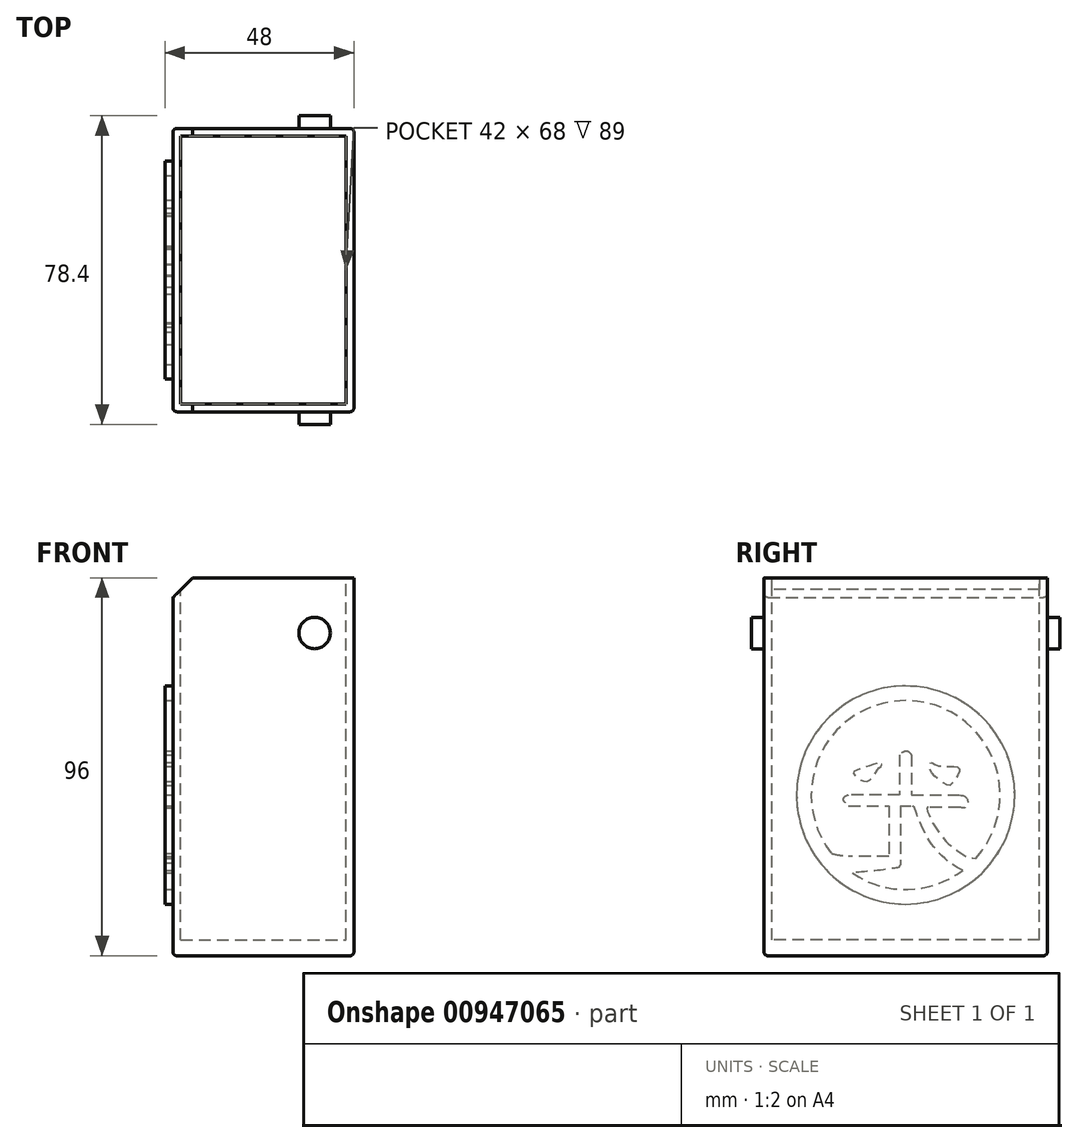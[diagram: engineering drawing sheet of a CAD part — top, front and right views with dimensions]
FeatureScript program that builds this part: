
annotation { "Feature Type Name" : "Feature", "Feature Type Description" : "" }
export const myFeature = defineFeature(function(context is Context, id is Id, definition is map)
    precondition{}
    {
        {
            var Q0;
            Q0=qCreatedBy(makeId("Top.planeOp"),FACE);
            var sketch = newSketch(context, id + "F0", { "sketchPlane" : qUnion([Q0])});
            skLineSegment(sketch, "E0.bottom", {"start": v(-23, 36) * mm, "end": v(23, 36) * mm});
            skLineSegment(sketch, "E0.top", {"start": v(-23, -36) * mm, "end": v(23, -36) * mm});
            skLineSegment(sketch, "E0.left", {"start": v(-23, 36) * mm, "end": v(-23, -36) * mm});
            skLineSegment(sketch, "E0.right", {"start": v(23, 36) * mm, "end": v(23, -36) * mm});
            skPoint(sketch, "E0.middle", {"position": v(0, 0) * mm});
            skSolve(sketch);
        }
        {
            var Q0;
            Q0 = qSketchRegion(id + "F0", true);
            extrude(context, id + "F1", {"entities" : qUnion([Q0]), "depth" : 96 * mm, "offsetDistance" : 25 * mm});
        }
        {
            var Q0;
            Q0=makeQuery(id+"F1.opExtrude","CAP_FACE",FACE,{"disambiguationData":[OSD([sQuery(id+"F0.wireOp",EDGE,"E0.bottom"),sQuery(id+"F0.wireOp",EDGE,"E0.top"),sQuery(id+"F0.wireOp",EDGE,"E0.left"),sQuery(id+"F0.wireOp",EDGE,"E0.right")])],"isStart":false});
            var sketch = newSketch(context, id + "F2", { "sketchPlane" : qUnion([Q0])});
            skLineSegment(sketch, "E1.bottom", {"start": v(-21, 34) * mm, "end": v(21, 34) * mm});
            skLineSegment(sketch, "E1.top", {"start": v(-21, -34) * mm, "end": v(21, -34) * mm});
            skLineSegment(sketch, "E1.left", {"start": v(-21, 34) * mm, "end": v(-21, -34) * mm});
            skLineSegment(sketch, "E1.right", {"start": v(21, 34) * mm, "end": v(21, -34) * mm});
            skPoint(sketch, "E1.middle", {"position": v(0, 0) * mm});
            skSolve(sketch);
        }
        {
            var Q0;
            Q0=makeQuery(id+"F2.imprint","IMPRINT",FACE,{"disambiguationData":[TD([[makeQuery(id+"F2.imprint","IMPRINT",EDGE,{"derivedFrom":sQuery(id+"F2.wireOp",EDGE,"E1.bottom")}),-1.0]])]});
            extrude(context, id + "F3", {"entities" : qUnion([Q0]), "operationType" : NewBodyOperationType.REMOVE, "oppositeDirection" : true, "depth" : 92 * mm, "offsetDistance" : 25 * mm});
        }
        {
            var Q0;
            Q0=makeQuery(id+"F1.opExtrude","SWEPT_FACE",FACE,{"disambiguationData":[OSD([sQuery(id+"F0.wireOp",EDGE,"E0.top")])]});
            var sketch = newSketch(context, id + "F4", { "sketchPlane" : qUnion([Q0])});
            skCircle(sketch, "E2", {"center": v(13, 82) * mm, "radius": 4 * mm});
            skSolve(sketch);
        }
        {
            var Q0;
            Q0 = qSketchRegion(id + "F4", true);
            extrude(context, id + "F5", {"entities" : qUnion([Q0]), "operationType" : NewBodyOperationType.ADD, "depth" : 3.2 * mm, "offsetDistance" : 25 * mm});
        }
        {
            var Q0;
            Q0=makeQuery(id+"F1.opExtrude","SWEPT_FACE",FACE,{"disambiguationData":[OSD([sQuery(id+"F0.wireOp",EDGE,"E0.bottom")])]});
            var sketch = newSketch(context, id + "F6", { "sketchPlane" : qUnion([Q0])});
            skCircle(sketch, "E3", {"center": v(-13, 82) * mm, "radius": 4 * mm});
            skSolve(sketch);
        }
        {
            var Q0;
            Q0 = qSketchRegion(id + "F6", true);
            extrude(context, id + "F7", {"entities" : qUnion([Q0]), "operationType" : NewBodyOperationType.ADD, "depth" : 3.2 * mm, "offsetDistance" : 25 * mm});
        }
        {
            var Q0;
            Q0=makeQuery(id+"F1.opExtrude","CAP_EDGE",EDGE,{"disambiguationData":[OSD([sQuery(id+"F0.wireOp",EDGE,"E0.left")])],"isStart":false});
            chamfer(context, id + "F8", {"entities" : qUnion([Q0]), "width" : 5 * mm, "tangentPropagation" : true});
        }
        {
            var Q0;
            Q0=makeQuery(id+"F1.opExtrude","SWEPT_EDGE",EDGE,{"disambiguationData":[OSD([sQuery(id+"F0.wireOp",EDGE,"E0.top"),sQuery(id+"F0.wireOp",EDGE,"E0.left")])]});
            var Q1;
            Q1=makeQuery(id+"F1.opExtrude","SWEPT_EDGE",EDGE,{"disambiguationData":[OSD([sQuery(id+"F0.wireOp",EDGE,"E0.top"),sQuery(id+"F0.wireOp",EDGE,"E0.right")])]});
            var Q2;
            Q2=makeQuery(id+"F1.opExtrude","SWEPT_EDGE",EDGE,{"disambiguationData":[OSD([sQuery(id+"F0.wireOp",EDGE,"E0.bottom"),sQuery(id+"F0.wireOp",EDGE,"E0.right")])]});
            var Q3;
            Q3=makeQuery(id+"F1.opExtrude","SWEPT_EDGE",EDGE,{"disambiguationData":[OSD([sQuery(id+"F0.wireOp",EDGE,"E0.bottom"),sQuery(id+"F0.wireOp",EDGE,"E0.left")])]});
            var Q4;
            Q4=makeQuery(id+"F1.opExtrude","CAP_EDGE",EDGE,{"disambiguationData":[OSD([sQuery(id+"F0.wireOp",EDGE,"E0.right")])],"isStart":true});
            var Q5;
            Q5=makeQuery(id+"F1.opExtrude","CAP_EDGE",EDGE,{"disambiguationData":[OSD([sQuery(id+"F0.wireOp",EDGE,"E0.left")])],"isStart":true});
            var Q6;
            Q6=makeQuery(id+"F1.opExtrude","CAP_EDGE",EDGE,{"disambiguationData":[OSD([sQuery(id+"F0.wireOp",EDGE,"E0.bottom")])],"isStart":true});
            var Q7;
            Q7=makeQuery(id+"F1.opExtrude","CAP_EDGE",EDGE,{"disambiguationData":[OSD([sQuery(id+"F0.wireOp",EDGE,"E0.top")])],"isStart":true});
            fillet(context, id + "F9", {"entities" : qUnion([Q0, Q1, Q2, Q3, Q4, Q5, Q6, Q7]), "radius" : 1 * mm, "tangentPropagation" : true, "allowEdgeOverflow" : false});
        }
        {
            var Q0;
            Q0=makeQuery(id+"F1.opExtrude","SWEPT_FACE",FACE,{"disambiguationData":[OSD([sQuery(id+"F0.wireOp",EDGE,"E0.left")])]});
            var sketch = newSketch(context, id + "F10", { "sketchPlane" : qUnion([Q0])});
            skFitSpline(sketch, "E4", {"points": [v(-13.17, 47.96) * mm, v(-13.57, 46.65) * mm, v(-11.86, 43.83) * mm, v(-10.86, 43.33) * mm, v(-6.83, 46.25) * mm, v(-6.08, 48.36) * mm, v(-6.53, 49.11) * mm, v(-8.14, 48.3) * mm, v(-13.17, 47.96) * mm]});
            skFitSpline(sketch, "E5", {"points": [v(7.24, 48.91) * mm, v(11.71, 47.45) * mm, v(13.27, 46.5) * mm, v(12.17, 45.1) * mm, v(9.75, 44.34) * mm, v(7.9, 46) * mm, v(6.89, 47.6) * mm, v(6.08, 48.46) * mm, v(6.44, 49.01) * mm, v(7.24, 48.91) * mm]});
            skLineSegment(sketch, "E6", {"start": v(-1.5, 51.07) * mm, "end": v(-1.5, 40.82) * mm});
            skLineSegment(sketch, "E7", {"start": v(-1.5, 40.82) * mm, "end": v(-13.82, 40.82) * mm});
            skLineSegment(sketch, "E8", {"start": v(1.56, 51.07) * mm, "end": v(1.56, 40.82) * mm});
            skLineSegment(sketch, "E9", {"start": v(1.56, 40.82) * mm, "end": v(14.48, 40.82) * mm});
            skLineSegment(sketch, "E10", {"start": v(14.48, 38.1) * mm, "end": v(4.27, 38.1) * mm});
            skLineSegment(sketch, "E11", {"start": v(4.27, 38.1) * mm, "end": v(4.27, 25.29) * mm});
            skLineSegment(sketch, "E12", {"start": v(4.27, 25.29) * mm, "end": v(14.48, 25.29) * mm});
            skLineSegment(sketch, "E13", {"start": v(1.3, 38.1) * mm, "end": v(1.3, 23.53) * mm});
            skLineSegment(sketch, "E14", {"start": v(-13.82, 37.7) * mm, "end": v(-5.83, 37.7) * mm});
            skLineSegment(sketch, "E15", {"start": v(1.3, 38.1) * mm, "end": v(-1.4, 38.1) * mm});
            skFitSpline(sketch, "E16", {"points": [v(-1.5, 51.07) * mm, v(-0.7, 51.83) * mm, v(0.4, 51.83) * mm, v(1.56, 51.07) * mm], "startDerivative": vector(2.25, 2.85) * mm, "endDerivative": vector(3.1, -2.53) * mm});
            skFitSpline(sketch, "E17", {"points": [v(14.48, 40.82) * mm, v(15.79, 40.11) * mm, v(15.79, 39.31) * mm, v(14.48, 38.1) * mm], "startDerivative": vector(4.6, -1.66) * mm, "endDerivative": vector(-4.2, -3.06) * mm});
            skFitSpline(sketch, "E18", {"points": [v(-13.82, 40.82) * mm, v(-15.18, 40.37) * mm, v(-15.78, 38.96) * mm, v(-15.13, 37.65) * mm, v(-13.82, 37.7) * mm], "startDerivative": vector(-5.95, -0.93) * mm, "endDerivative": vector(5.94, 1.53) * mm});
            skFitSpline(sketch, "E19", {"points": [v(-5.83, 37.7) * mm, v(-5.43, 37.7) * mm, v(-5.83, 36) * mm, v(-6.83, 33.78) * mm, v(-8.84, 30.77) * mm, v(-10.86, 28.5) * mm, v(-13.42, 26.5) * mm, v(-15.98, 25.04) * mm, v(-18.4, 24.68) * mm, v(-19.1, 24.23) * mm, v(-19.05, 22.17) * mm, v(-16.64, 21.27) * mm, v(-14.32, 21.82) * mm, v(-11.36, 23.58) * mm, v(-8.04, 26.6) * mm, v(-5.43, 30.26) * mm, v(-2.76, 36.2) * mm, v(-2.16, 37.7) * mm, v(-1.4, 38.1) * mm], "startDerivative": vector(22.56, 6.42) * mm, "endDerivative": vector(26.13, 9.2) * mm});
            skFitSpline(sketch, "E20", {"points": [v(1.3, 23.53) * mm, v(1.76, 22.47) * mm, v(3.07, 22.22) * mm, v(4.38, 22.02) * mm, v(8.3, 21.52) * mm, v(12.22, 21.16) * mm, v(18.15, 21.11) * mm, v(19.96, 23.53) * mm, v(19.76, 26.24) * mm, v(18.95, 26.04) * mm, v(14.48, 25.29) * mm], "startDerivative": vector(3.67, -19.1) * mm, "endDerivative": vector(-40.54, -4.42) * mm});
            skCircle(sketch, "E21", {"center": v(0, 40.82) * mm, "radius": 24 * mm});
            skCircle(sketch, "E22", {"center": v(0, 40.82) * mm, "radius": 27.72 * mm});
            skSolve(sketch);
        }
        {
            var Q0;
            Q0=makeQuery(id+"F10.imprint","IMPRINT",FACE,{"disambiguationData":[TD([[makeQuery(id+"F10.imprint","IMPRINT",EDGE,{"derivedFrom":sQuery(id+"F10.wireOp",EDGE,"E22")}),1.0]])]});
            var Q1;
            Q1=makeQuery(id+"F10.imprint","IMPRINT",FACE,{"disambiguationData":[TD([[makeQuery(id+"F10.imprint","IMPRINT",EDGE,{"derivedFrom":sQuery(id+"F10.wireOp",EDGE,"E4")}),1.0]])]});
            var Q2;
            Q2=makeQuery(id+"F10.imprint","IMPRINT",FACE,{"disambiguationData":[TD([[makeQuery(id+"F10.imprint","IMPRINT",EDGE,{"derivedFrom":sQuery(id+"F10.wireOp",EDGE,"E6")}),1.0]])]});
            var Q3;
            Q3=makeQuery(id+"F10.imprint","IMPRINT",FACE,{"disambiguationData":[TD([[makeQuery(id+"F10.imprint","IMPRINT",EDGE,{"derivedFrom":sQuery(id+"F10.wireOp",EDGE,"E5")}),-1.0]])]});
            var Q4;
            {var subQ0=sQuery(id+"F10.wireOp",EDGE,"E21");var subQ1=sQuery(id+"F10.wireOp",EDGE,"E19");var subQ2=makeQuery(id+"F10.imprint","INTERSECT",VERTEX,{"disambiguationData":[OD(0.0)],"derivedFrom":[subQ1,subQ0]});Q4=makeQuery(id+"F10.imprint","IMPRINT",FACE,{"disambiguationData":[TD([[makeQuery(id+"F10.imprint","IMPRINT",EDGE,{"disambiguationData":[TD([[subQ2,-1.0]])],"derivedFrom":subQ1}),1.0]])]});}
            var Q5;
            {var subQ0=sQuery(id+"F10.wireOp",EDGE,"E21");var subQ1=sQuery(id+"F10.wireOp",EDGE,"E20");var subQ2=makeQuery(id+"F10.imprint","INTERSECT",VERTEX,{"disambiguationData":[OD(0.0)],"derivedFrom":[subQ1,subQ0]});Q5=makeQuery(id+"F10.imprint","IMPRINT",FACE,{"disambiguationData":[TD([[makeQuery(id+"F10.imprint","IMPRINT",EDGE,{"disambiguationData":[TD([[subQ2,-1.0]])],"derivedFrom":subQ1}),1.0]])]});}
            extrude(context, id + "F11", {"entities" : qUnion([Q0, Q1, Q2, Q3, Q4, Q5]), "operationType" : NewBodyOperationType.ADD, "depth" : 2 * mm, "offsetDistance" : 25 * mm});
        }
    });
